# Revit family: 1Electronics_Commercial-Audio_Biamp_Music-Source_PC3000
name_source: partatom
category: Communication Devices
units: mm (PartAtom-declared; Revit-internal decimal feet)

## family parameters
Cut with Voids When Loaded = No
Host = Face
Maintain Annotation Orientation = No
OmniClass Number = 23.85.10.11.14
OmniClass Title = Audio Equipment
Part Type = Normal
Room Calculation Point = No
Round Connector Dimension = Use Diameter
Shared = No

## types (1)
- PCR3000RMKIII
    Apparent Load = 0 VA
    Applicable low impedance = Yes
    Bluetooth = Yes
    CD = Yes
    Connector Description = 230VAC / 50-60Hz / 30W
    DAB Tuner / DAB + = Yes
    Default Elevation = 4' - 0"
    Depth = 1' - 0"
    Description = PCR3000RMKIII Music Source with DAB & FM RDS/CD/USB/SD-Card /Bluetooth
    FM tuner = Yes
    Height = 0' - 1 1/2"
    Housing Material = Biamp - Metal - Black
    IR remote included = Yes
    Manufacturer = Biamp
    Max Power Consumption = 0 W
    Model = PCR3000RMKIII
    Number of Poles = 1
    Other/digital outputs = 1 x optical + 1 x coaxial
    Power Factor = 1
    Product Documentation Link = https://downloads.biamp.com
    Product Page URL = https://www.biamp.com
    Product data url = https://www.bimobject.com
    RS232 control = Yes
    SD card = 32 GB up to 9999 songs
    Supported bluetooth profiles = A2DP, AVRCP and SPP
    Supported file format = MP3, WMA
    URL = https://www.biamp.com
    USB = 32 GB up to 9999 songs
    Unbalanced outputs = 2 x RCA + COMBI RCA
    Voltage = 230 V
    Weight = 10.15 lbf
    Width = 1' - 7"

## geometry (parser evidence)
native form markers: Sweep x4
no freeform markers — native parametric forms only
